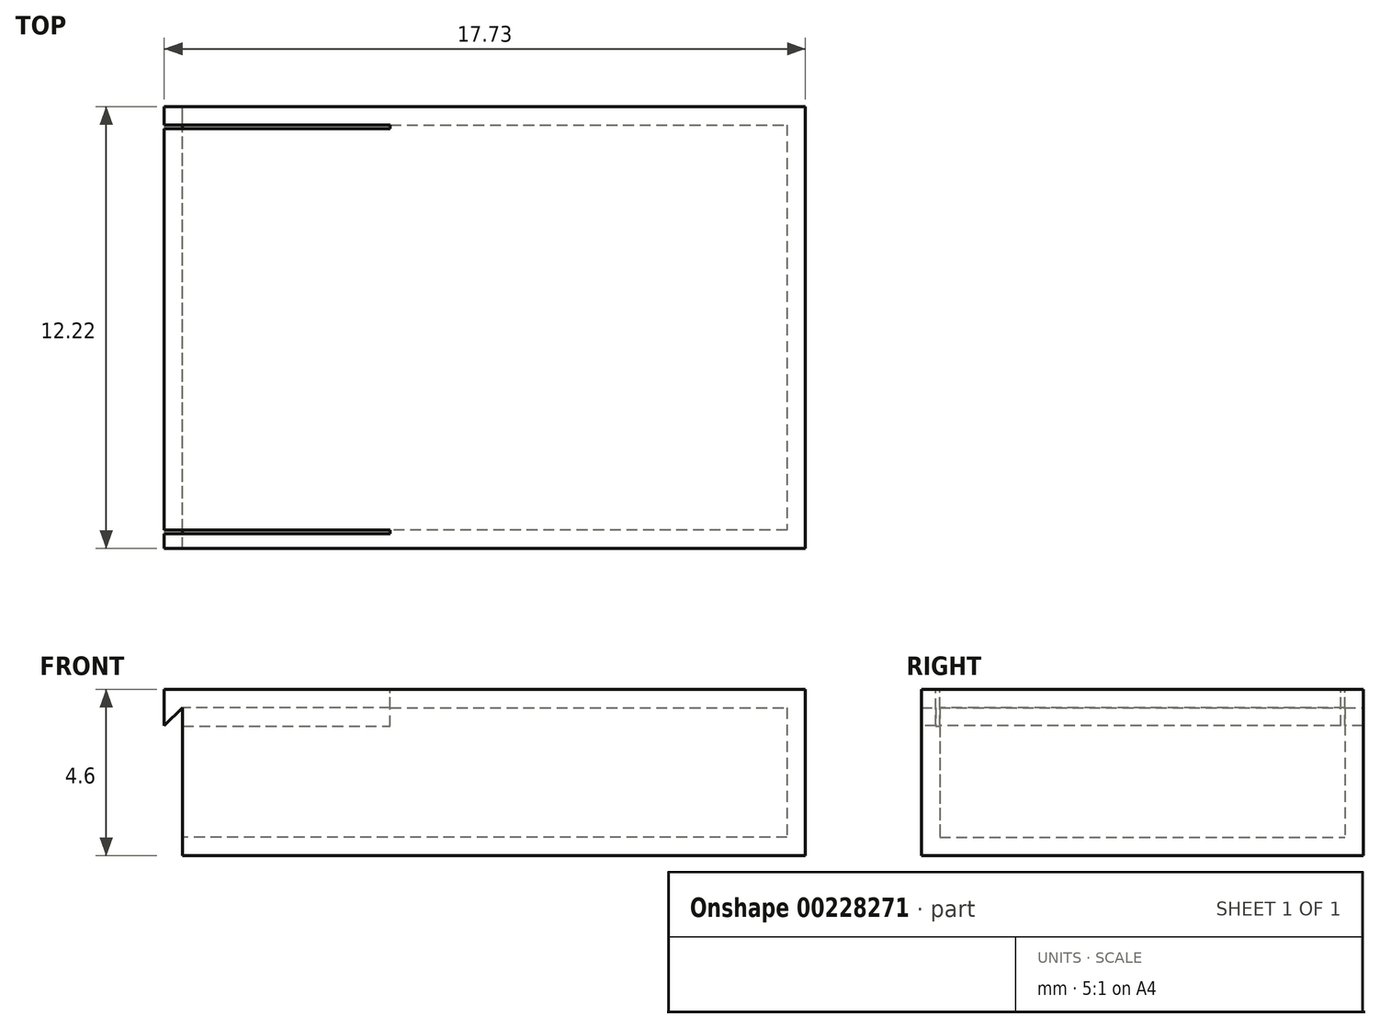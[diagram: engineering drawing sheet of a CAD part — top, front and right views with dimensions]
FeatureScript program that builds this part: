
annotation { "Feature Type Name" : "Feature", "Feature Type Description" : "" }
export const myFeature = defineFeature(function(context is Context, id is Id, definition is map)
    precondition{}
    {
        {
            var Q0;
            Q0=qCreatedBy(makeId("Top.planeOp"),FACE);
            var sketch = newSketch(context, id + "F0", { "sketchPlane" : qUnion([Q0])});
            skLineSegment(sketch, "E0", {"start": v(-1.48, -17.26) * mm, "end": v(-1.48, -5.04) * mm});
            skLineSegment(sketch, "E1", {"start": v(-1.48, -5.04) * mm, "end": v(15.74, -5.04) * mm});
            skLineSegment(sketch, "E2", {"start": v(15.74, -5.04) * mm, "end": v(15.74, -17.26) * mm});
            skLineSegment(sketch, "E3", {"start": v(15.74, -17.26) * mm, "end": v(-1.48, -17.26) * mm});
            skSolve(sketch);
        }
        {
            var Q0;
            Q0 = qSketchRegion(id + "F0", true);
            extrude(context, id + "F1", {"entities" : qUnion([Q0]), "depth" : 4.6 * mm});
        }
        {
            var Q0;
            Q0=makeQuery(id+"F1.opExtrude","SWEPT_FACE",FACE,{"disambiguationData":[OSD([sQuery(id+"F0.wireOp",EDGE,"E0")])]});
            shell(context, id + "F2", {"entities" : qUnion([Q0]), "thickness" : 0.5 * mm});
        }
        {
            var Q0;
            Q0=makeQuery(id+"F1.opExtrude","SWEPT_FACE",FACE,{"disambiguationData":[OSD([sQuery(id+"F0.wireOp",EDGE,"E3")])]});
            var sketch = newSketch(context, id + "F3", { "sketchPlane" : qUnion([Q0])});
            skLineSegment(sketch, "E4", {"start": v(-1.48, 4.6) * mm, "end": v(-1.99, 4.6) * mm});
            skLineSegment(sketch, "E5", {"start": v(-1.99, 4.6) * mm, "end": v(-1.99, 3.6) * mm});
            skLineSegment(sketch, "E6", {"start": v(-1.99, 3.6) * mm, "end": v(-1.48, 4.1) * mm});
            skPoint(sketch, "E7", {"position": v(-1.99, 4.1) * mm});
            skSolve(sketch);
        }
        {
            var Q0;
            {var subQ0=sQuery(id+"F3.wireOp",EDGE,"E4");Q0=makeQuery(id+"F3.imprint","IMPRINT",FACE,{"disambiguationData":[TD([[makeQuery(id+"F3.imprint","IMPRINT",EDGE,{"derivedFrom":subQ0}),1.0]])]});}
            extrude(context, id + "F4", {"entities" : qUnion([Q0]), "operationType" : NewBodyOperationType.ADD, "oppositeDirection" : true, "depth" : 12.22 * mm});
        }
        {
            var Q0;
            Q0=makeQuery(id+"F4.boolean.opBoolean","MERGE",FACE,{"derivedFrom":[makeQuery(id+"F1.opExtrude","CAP_FACE",FACE,{"disambiguationData":[OSD([sQuery(id+"F0.wireOp",EDGE,"E0"),sQuery(id+"F0.wireOp",EDGE,"E1"),sQuery(id+"F0.wireOp",EDGE,"E2"),sQuery(id+"F0.wireOp",EDGE,"E3")])],"isStart":false}),makeQuery(id+"F4.opExtrude","SWEPT_FACE",FACE,{"disambiguationData":[OSD([sQuery(id+"F3.wireOp",EDGE,"E4")])]})]});
            var sketch = newSketch(context, id + "F5", { "sketchPlane" : qUnion([Q0])});
            skLineSegment(sketch, "E8", {"start": v(-1.99, -16.75) * mm, "end": v(4.26, -16.75) * mm});
            skLineSegment(sketch, "E9", {"start": v(4.26, -16.85) * mm, "end": v(4.26, -16.75) * mm});
            skLineSegment(sketch, "E10", {"start": v(4.26, -16.85) * mm, "end": v(-1.99, -16.85) * mm});
            skLineSegment(sketch, "E11", {"start": v(-1.99, -16.75) * mm, "end": v(-1.99, -16.85) * mm});
            skLineSegment(sketch, "E12", {"start": v(-1.99, -5.55) * mm, "end": v(4.26, -5.55) * mm});
            skLineSegment(sketch, "E13", {"start": v(4.26, -5.55) * mm, "end": v(4.26, -5.65) * mm});
            skLineSegment(sketch, "E14", {"start": v(4.26, -5.65) * mm, "end": v(-1.99, -5.65) * mm});
            skLineSegment(sketch, "E15", {"start": v(-1.99, -5.65) * mm, "end": v(-1.99, -5.55) * mm});
            skSolve(sketch);
        }
        {
            var Q0;
            Q0=makeQuery(id+"F5.imprint","IMPRINT",FACE,{"disambiguationData":[TD([[makeQuery(id+"F5.imprint","IMPRINT",EDGE,{"derivedFrom":sQuery(id+"F5.wireOp",EDGE,"E12")}),-1.0]])]});
            var Q1;
            Q1=makeQuery(id+"F5.imprint","IMPRINT",FACE,{"disambiguationData":[TD([[makeQuery(id+"F5.imprint","IMPRINT",EDGE,{"derivedFrom":sQuery(id+"F5.wireOp",EDGE,"E8")}),-1.0]])]});
            extrude(context, id + "F6", {"entities" : qUnion([Q0, Q1]), "operationType" : NewBodyOperationType.REMOVE, "oppositeDirection" : true, "depth" : 1.02 * mm});
        }
    });
